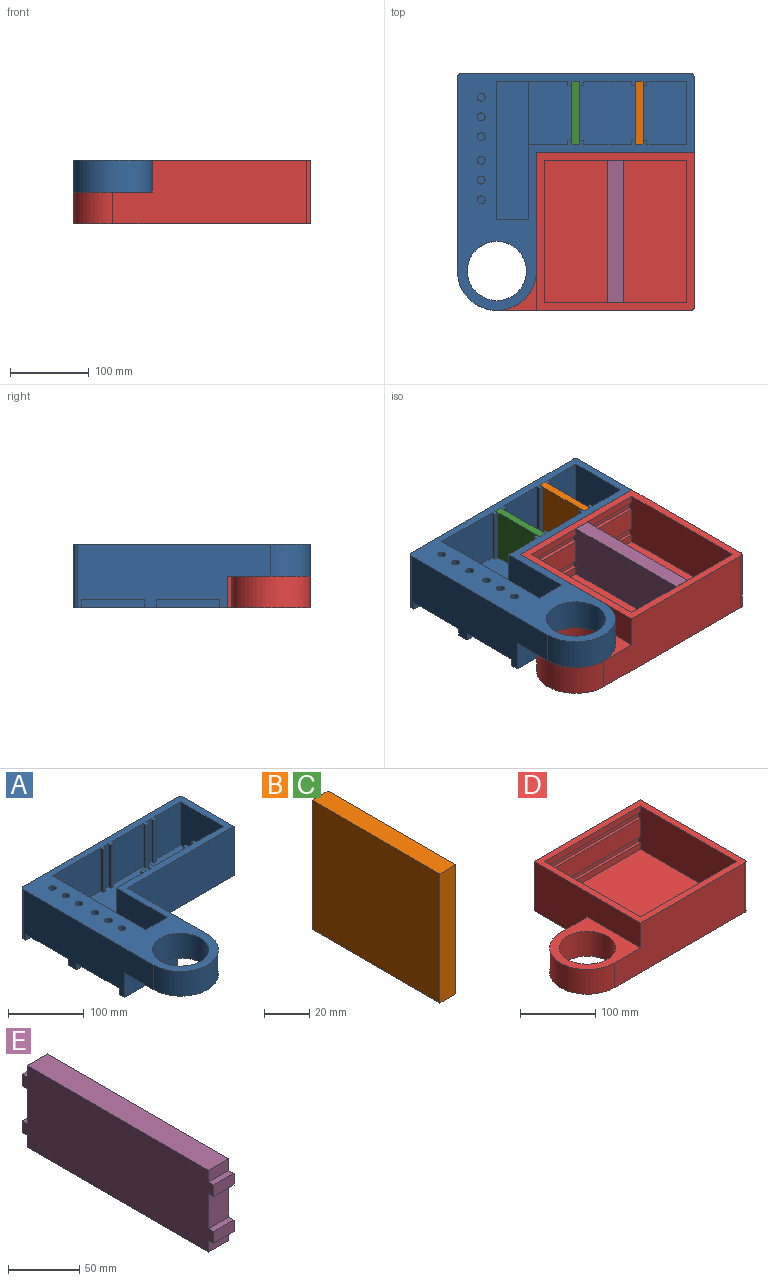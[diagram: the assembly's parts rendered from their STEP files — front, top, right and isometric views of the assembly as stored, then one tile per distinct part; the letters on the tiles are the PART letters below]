
ASSEMBLY  parts=5 mates=4
PART A: 74 faces, bbox 300x300x80 mm
  f0: plane 75x10mm, normal (0,-1,0), area 750mm2, adj f4,f6,f17,f73
  f1: plane 75x10mm, normal (0,1,0), area 750mm2, adj f5,f6,f17,f72
  f2: plane 75x10mm, normal (0,1,0), area 750mm2, adj f4,f6,f17,f73
  f3: plane 75x10mm, normal (0,-1,0), area 750mm2, adj f5,f6,f17,f72
  f4: plane 80x75mm, normal (0,0,-1), area 6000mm2, adj f0,f2,f6,f73
  f5: plane 80x75mm, normal (0,0,-1), area 6000mm2, adj f1,f3,f6,f72
  f6: plane 245x80mm, normal (-1,0,0), area 15800mm2, adj f0,f1,f2,f3,f4,f5,f17,f26
  f7: plane 70x60mm, normal (0,1,0), area 4200mm2, adj f16,f26,f33,f42
  f8: plane 70x10mm, normal (0,1,0), area 700mm2, adj f16,f26,f37,f41
  f9: plane 70x10mm, normal (0,-1,0), area 700mm2, adj f16,f26,f50,f53
  f10: plane 70x60mm, normal (0,-1,0), area 4200mm2, adj f16,f26,f44,f51
  f11: plane 90x70mm, normal (0,-1,0), area 5500mm2, adj f16,f26,f46,f57,f64,f71
  f12: plane 70x10mm, normal (0,-1,0), area 700mm2, adj f16,f26,f45,f48
  f13: plane 70x50mm, normal (0,1,0), area 3500mm2, adj f16,f25,f26,f34
  f14: plane 70x10mm, normal (0,1,0), area 700mm2, adj f16,f26,f31,f36
  f15: plane 70x50mm, normal (0,-1,0), area 3500mm2, adj f16,f25,f26,f52
  f16: plane 200x80mm, normal (0,0,1), area 15800mm2, adj f7,f8,f9,f10,f11,f12,f13,f14
  f17: plane 300x195mm, normal (0,0,-1), area 27489.3mm2, adj f0,f1,f2,f3,f6,f18,f19,f20
  f18: plane 150x80mm, normal (1,0,0), area 9800mm2, adj f17,f19,f26,f27,f29,f30
  f19: plane 200x80mm, normal (0,-1,0), area 16000mm2, adj f17,f18,f20,f26
  f20: plane 95x80mm, normal (1,0,0), area 7600mm2, adj f17,f19,f26,f55
  f21: plane 290x80mm, normal (0,1,0), area 23200mm2, adj f17,f26,f55,f56
  f22: plane 70x50mm, normal (0,1,0), area 3500mm2, adj f16,f23,f26,f39,f57
  f23: plane 95x50mm, normal (-1,0,0), area 4750mm2, adj f22,f24,f26,f71
  f24: plane 50x40mm, normal (0,1,0), area 2000mm2, adj f23,f26,f64,f71
  f25: plane 80x70mm, normal (-1,0,0), area 5600mm2, adj f13,f15,f16,f26
  f26: plane 300x300mm, normal (0,0,1), area 21227.2mm2, adj f6,f7,f8,f9,f10,f11,f12,f13
  f27: cylinder r=50mm len=100mm, axis (0,0,-1), area 6283.2mm2, adj f6,f18,f26,f30
  f28: cylinder r=37.5mm len=75mm, axis (0,0,-1), area 9424.8mm2, adj f26,f30
  f29: plane 100x40mm, normal (0,-1,0), area 4000mm2, adj f6,f17,f18,f30
  f30: plane 105x100mm, normal (0,0,-1), area 5009.1mm2, adj f6,f18,f27,f28,f29
  f31: plane 70x5mm, normal (1,0,0), area 350mm2, adj f14,f16,f26,f32
  f32: plane 70x5mm, normal (0,1,0), area 350mm2, adj f16,f26,f31,f33
  f33: plane 70x5mm, normal (-1,0,0), area 350mm2, adj f7,f16,f26,f32
  f34: plane 70x5mm, normal (1,0,0), area 350mm2, adj f13,f16,f26,f35
  f35: plane 70x5mm, normal (0,1,0), area 350mm2, adj f16,f26,f34,f36
  f36: plane 70x5mm, normal (-1,0,0), area 350mm2, adj f14,f16,f26,f35
  f37: plane 70x5mm, normal (1,0,0), area 350mm2, adj f8,f16,f26,f38
  f38: plane 70x5mm, normal (0,1,0), area 350mm2, adj f16,f26,f37,f39
  f39: plane 70x5mm, normal (-1,0,0), area 350mm2, adj f16,f22,f26,f38
  f40: plane 70x5mm, normal (0,1,0), area 350mm2, adj f16,f26,f41,f42
  f41: plane 70x5mm, normal (-1,0,0), area 350mm2, adj f8,f16,f26,f40
  f42: plane 70x5mm, normal (1,0,0), area 350mm2, adj f7,f16,f26,f40
  f43: plane 70x5mm, normal (0,-1,0), area 350mm2, adj f16,f26,f44,f45
  f44: plane 70x5mm, normal (1,0,0), area 350mm2, adj f10,f16,f26,f43
  f45: plane 70x5mm, normal (-1,0,0), area 350mm2, adj f12,f16,f26,f43
  f46: plane 70x5mm, normal (-1,0,0), area 350mm2, adj f11,f16,f26,f47
  f47: plane 70x5mm, normal (0,-1,0), area 350mm2, adj f16,f26,f46,f48
  f48: plane 70x5mm, normal (1,0,0), area 350mm2, adj f12,f16,f26,f47
  f49: plane 70x5mm, normal (0,-1,0), area 350mm2, adj f16,f26,f50,f51
  f50: plane 70x5mm, normal (1,0,0), area 350mm2, adj f9,f16,f26,f49
  f51: plane 70x5mm, normal (-1,0,0), area 350mm2, adj f10,f16,f26,f49
  f52: plane 70x5mm, normal (1,0,0), area 350mm2, adj f15,f16,f26,f54
  f53: plane 70x5mm, normal (-1,0,0), area 350mm2, adj f9,f16,f26,f54
  f54: plane 70x5mm, normal (0,-1,0), area 350mm2, adj f16,f26,f52,f53
  f55: cylinder r=5mm len=80mm, axis (0,0,1), area 628.3mm2, adj f17,f20,f21,f26
  f56: cylinder r=5mm len=80mm, axis (0,0,-1), area 628.3mm2, adj f6,f17,f21,f26
  f57: plane 80x20mm, normal (1,0,0), area 1600mm2, adj f11,f16,f22,f71
  f58: cylinder r=5mm len=65mm, axis (0,0,-1), area 2042mm2, adj f26,f70
  f59: cylinder r=5mm len=65mm, axis (0,0,-1), area 2042mm2, adj f26,f65
  f60: cylinder r=5mm len=65mm, axis (0,0,-1), area 2042mm2, adj f26,f66
  f61: cylinder r=5mm len=65mm, axis (0,0,-1), area 2042mm2, adj f26,f67
  f62: cylinder r=5mm len=65mm, axis (0,0,-1), area 2042mm2, adj f26,f68
  f63: cylinder r=5mm len=65mm, axis (0,0,-1), area 2042mm2, adj f26,f69
  f64: plane 175x50mm, normal (1,0,0), area 8750mm2, adj f11,f24,f26,f71
  f65: plane 10x10mm, normal (0,0,1), area 78.5mm2, adj f59
  f66: plane 10x10mm, normal (0,0,1), area 78.5mm2, adj f60
  f67: plane 10x10mm, normal (0,0,1), area 78.5mm2, adj f61
  f68: plane 10x10mm, normal (0,0,1), area 78.5mm2, adj f62
  f69: plane 10x10mm, normal (0,0,1), area 78.5mm2, adj f63
  f70: plane 10x10mm, normal (0,0,1), area 78.5mm2, adj f58
  f71: plane 175x40mm, normal (0,0,1), area 7000mm2, adj f11,f23,f24,f57,f64
  f72: plane 80x10mm, normal (-1,0,0), area 800mm2, adj f1,f3,f5,f17
  f73: plane 80x10mm, normal (-1,0,0), area 800mm2, adj f0,f2,f4,f17
PART B: 6 faces, bbox 10x80x70 mm
  f0: plane 70x10mm, normal (0,-1,0), area 700mm2, adj f1,f3,f4,f5
  f1: plane 80x70mm, normal (1,0,0), area 5600mm2, adj f0,f2,f4,f5
  f2: plane 70x10mm, normal (0,1,0), area 700mm2, adj f1,f3,f4,f5
  f3: plane 80x70mm, normal (-1,0,0), area 5600mm2, adj f0,f2,f4,f5
  f4: plane 80x10mm, normal (0,0,1), area 800mm2, adj f0,f1,f2,f3
  f5: plane 80x10mm, normal (0,0,-1), area 800mm2, adj f0,f1,f2,f3
PART C: same geometry as B
PART D: 32 faces, bbox 300.3x200x80 mm
  f0: plane 180.27x10mm, normal (0,1,0), area 1802.7mm2, adj f7,f9,f12,f29
  f1: plane 180.27x30mm, normal (0,1,0), area 5408.1mm2, adj f7,f9,f27,f30
  f2: plane 180.27x10mm, normal (0,-1,0), area 1802.7mm2, adj f7,f9,f18,f23
  f3: plane 180.27x30mm, normal (0,-1,0), area 5408.1mm2, adj f7,f9,f21,f24
  f4: plane 200x80mm, normal (-1,0,0), area 12000mm2, adj f5,f11,f12,f13,f14,f17
  f5: plane 245.27x80mm, normal (0,-1,0), area 17621.7mm2, adj f4,f12,f13,f15,f17,f19
  f6: plane 195x80mm, normal (1,0,0), area 15600mm2, adj f11,f12,f13,f19
  f7: plane 190x70mm, normal (1,0,0), area 12800mm2, adj f0,f1,f2,f3,f8,f10,f12,f18
  f8: plane 180.27x10mm, normal (0,-1,0), area 1802.7mm2, adj f7,f9,f12,f20
  f9: plane 190x70mm, normal (-1,0,0), area 12800mm2, adj f0,f1,f2,f3,f8,f10,f12,f18
  f10: plane 180.27x10mm, normal (0,1,0), area 1802.7mm2, adj f7,f9,f18,f26
  f11: plane 200.27x80mm, normal (0,1,0), area 16021.7mm2, adj f4,f6,f12,f13
  f12: plane 200.27x200mm, normal (0,0,1), area 7600.1mm2, adj f0,f4,f5,f6,f7,f8,f9,f11
  f13: plane 300.27x200mm, normal (0,0,-1), area 44558mm2, adj f4,f5,f6,f11,f14,f15,f16,f19
  f14: plane 50x40mm, normal (0,1,0), area 2000mm2, adj f4,f13,f15,f17
  f15: cylinder r=50mm len=100mm, axis (0,0,-1), area 6283.2mm2, adj f5,f13,f14,f17
  f16: cylinder r=37.5mm len=75mm, axis (0,0,-1), area 9424.8mm2, adj f13,f17
  f17: plane 100x100mm, normal (0,0,1), area 4509.1mm2, adj f4,f5,f14,f15,f16
  f18: plane 180.27x180mm, normal (0,0,1), area 32448.8mm2, adj f2,f7,f9,f10
  f19: cylinder r=5mm len=80mm, axis (0,0,-1), area 628.3mm2, adj f5,f6,f12,f13
  f20: plane 180.27x5mm, normal (0,0,-1), area 901.4mm2, adj f7,f8,f9,f22
  f21: plane 180.27x5mm, normal (0,0,1), area 901.4mm2, adj f3,f7,f9,f22
  f22: plane 180.27x10mm, normal (0,-1,0), area 1802.7mm2, adj f7,f9,f20,f21
  f23: plane 180.27x5mm, normal (0,0,1), area 901.4mm2, adj f2,f7,f9,f25
  f24: plane 180.27x5mm, normal (0,0,-1), area 901.4mm2, adj f3,f7,f9,f25
  f25: plane 180.27x10mm, normal (0,-1,0), area 1802.7mm2, adj f7,f9,f23,f24
  f26: plane 180.27x5mm, normal (0,0,1), area 901.4mm2, adj f7,f9,f10,f28
  f27: plane 180.27x5mm, normal (0,0,-1), area 901.4mm2, adj f1,f7,f9,f28
  f28: plane 180.27x10mm, normal (0,1,0), area 1802.7mm2, adj f7,f9,f26,f27
  f29: plane 180.27x5mm, normal (0,0,-1), area 901.4mm2, adj f0,f7,f9,f31
  f30: plane 180.27x5mm, normal (0,0,1), area 901.4mm2, adj f1,f7,f9,f31
  f31: plane 180.27x10mm, normal (0,1,0), area 1802.7mm2, adj f7,f9,f29,f30
PART E: 22 faces, bbox 20x190x70 mm
  f0: plane 20x10mm, normal (0,1,0), area 200mm2, adj f5,f7,f9,f19
  f1: plane 30x20mm, normal (0,1,0), area 600mm2, adj f5,f7,f17,f20
  f2: plane 30x20mm, normal (0,-1,0), area 600mm2, adj f5,f7,f11,f14
  f3: plane 20x10mm, normal (0,-1,0), area 200mm2, adj f5,f7,f8,f10
  f4: plane 20x10mm, normal (0,-1,0), area 200mm2, adj f5,f7,f9,f13
  f5: plane 190x70mm, normal (1,0,0), area 12800mm2, adj f0,f1,f2,f3,f4,f6,f8,f9
  f6: plane 20x10mm, normal (0,1,0), area 200mm2, adj f5,f7,f8,f16
  f7: plane 190x70mm, normal (-1,0,0), area 12800mm2, adj f0,f1,f2,f3,f4,f6,f8,f9
  f8: plane 180x20mm, normal (0,0,1), area 3600mm2, adj f3,f5,f6,f7
  f9: plane 180x20mm, normal (0,0,-1), area 3600mm2, adj f0,f4,f5,f7
  f10: plane 20x5mm, normal (0,0,1), area 100mm2, adj f3,f5,f7,f12
  f11: plane 20x5mm, normal (0,0,-1), area 100mm2, adj f2,f5,f7,f12
  f12: plane 20x10mm, normal (0,-1,0), area 200mm2, adj f5,f7,f10,f11
  f13: plane 20x5mm, normal (0,0,-1), area 100mm2, adj f4,f5,f7,f15
  f14: plane 20x5mm, normal (0,0,1), area 100mm2, adj f2,f5,f7,f15
  f15: plane 20x10mm, normal (0,-1,0), area 200mm2, adj f5,f7,f13,f14
  f16: plane 20x5mm, normal (0,0,1), area 100mm2, adj f5,f6,f7,f18
  f17: plane 20x5mm, normal (0,0,-1), area 100mm2, adj f1,f5,f7,f18
  f18: plane 20x10mm, normal (0,1,0), area 200mm2, adj f5,f7,f16,f17
  f19: plane 20x5mm, normal (0,0,-1), area 100mm2, adj f0,f5,f7,f21
  f20: plane 20x5mm, normal (0,0,1), area 100mm2, adj f1,f5,f7,f21
  f21: plane 20x10mm, normal (0,1,0), area 200mm2, adj f5,f7,f19,f20
PLACE A t=(320.71,165.22,35.58)mm
PLACE B t=(555.71,375.22,45.58)mm fixed
PLACE C t=(475.71,375.22,45.58)mm fixed
PLACE D t=(479.51,301.43,35.58)mm
PLACE E t=(530.71,175.22,45.58)mm
MATE slider B.f0 <-> A.f14  axis (0,-1,0) through (550.71,375.22,80.58)mm
MATE slider E.f7 <-> D.f7  axis (-1,0,0) through (510.71,265.22,80.58)mm
MATE slider C.f0 <-> A.f8  axis (0,-1,0) through (470.71,375.22,80.58)mm
MATE revolute D.f15 <-> A.f27  axis (0,0,1) through (370.71,215.22,75.58)mm
